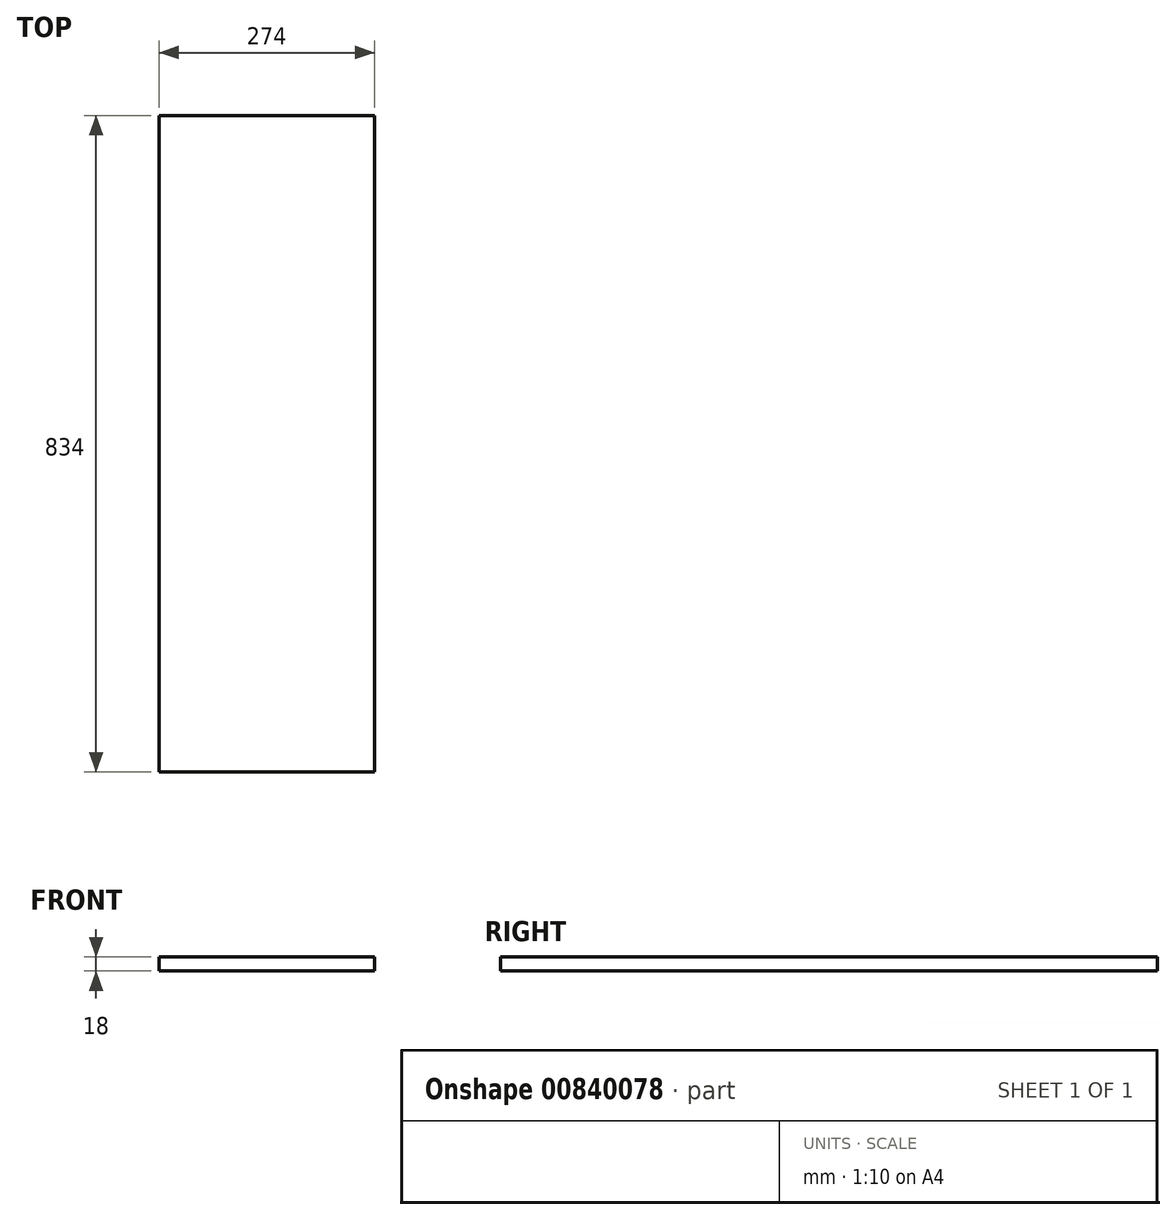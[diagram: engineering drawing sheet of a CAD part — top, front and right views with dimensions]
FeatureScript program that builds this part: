
annotation { "Feature Type Name" : "Feature", "Feature Type Description" : "" }
export const myFeature = defineFeature(function(context is Context, id is Id, definition is map)
    precondition{}
    {
        {
            var Q0;
            Q0=qCreatedBy(makeId("Top.planeOp"),FACE);
            var sketch = newSketch(context, id + "F0", { "sketchPlane" : qUnion([Q0])});
            skLineSegment(sketch, "E0.bottom", {"start": v(-137, -417) * mm, "end": v(137, -417) * mm});
            skLineSegment(sketch, "E0.top", {"start": v(-137, 417) * mm, "end": v(137, 417) * mm});
            skLineSegment(sketch, "E0.left", {"start": v(-137, -417) * mm, "end": v(-137, 417) * mm});
            skLineSegment(sketch, "E0.right", {"start": v(137, -417) * mm, "end": v(137, 417) * mm});
            skPoint(sketch, "E0.middle", {"position": v(0, 0) * mm});
            skSolve(sketch);
        }
        {
            var Q0;
            Q0=qSketchRegion(id+"F0",true);
            extrude(context, id + "F1", {"entities" : qUnion([Q0]), "oppositeDirection" : true, "depth" : 18 * mm, "offsetDistance" : 25 * mm});
        }
    });
